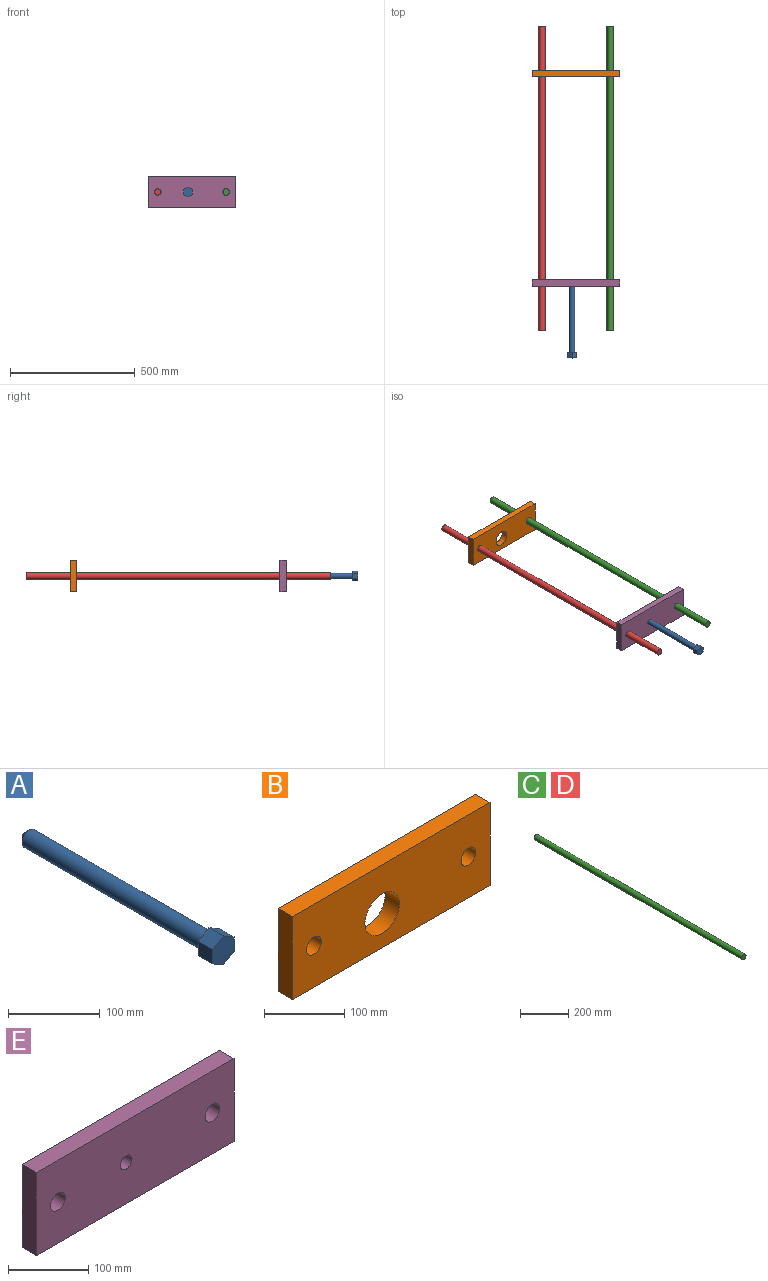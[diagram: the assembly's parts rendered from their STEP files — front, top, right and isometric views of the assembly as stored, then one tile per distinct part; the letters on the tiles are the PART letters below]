
ASSEMBLY  parts=5 mates=4
PART A: 11 faces, bbox 33.3x304.8x38.5 mm
  f0: cylinder r=11.11mm len=276.62mm, axis (0,1,0), area 19314.3mm2, adj f7,f9
  f1: plane 21.83x16.67mm, normal (0.5,0,0.87), area 420.1mm2, adj f2,f6,f7,f8
  f2: plane 21.83x16.67mm, normal (-0.5,0,0.87), area 420.1mm2, adj f1,f3,f7,f8
  f3: plane 21.83x19.25mm, normal (-1,0,0), area 420.1mm2, adj f2,f4,f7,f8
  f4: plane 21.83x16.67mm, normal (-0.5,0,-0.87), area 420.1mm2, adj f3,f5,f7,f8
  f5: plane 21.83x16.67mm, normal (0.5,0,-0.87), area 420.1mm2, adj f4,f6,f7,f8
  f6: plane 21.83x19.25mm, normal (1,0,0), area 420.1mm2, adj f1,f5,f7,f8
  f7: plane 38.5x33.34mm, normal (0,1,0), area 574.5mm2, adj f0,f1,f2,f3,f4,f5,f6
  f8: plane 38.5x33.34mm, normal (0,-1,0), area 962.5mm2, adj f1,f2,f3,f4,f5,f6
  f9: cone r=11.11mm half-angle=45deg, axis (0,-1,0), area 447.9mm2, adj f0,f10
  f10: plane 9.53x9.53mm, normal (0,1,0), area 71.3mm2, adj f9
PART B: 9 faces, bbox 349.3x25.4x127 mm
  f0: plane 349.25x25.4mm, normal (0,0,-1), area 8870.9mm2, adj f1,f6,f7,f8
  f1: plane 127x25.4mm, normal (1,0,0), area 3225.8mm2, adj f0,f2,f7,f8
  f2: plane 349.25x25.4mm, normal (0,0,1), area 8870.9mm2, adj f1,f6,f7,f8
  f3: cylinder r=13.09mm len=26.19mm, axis (0,1,0), area 2089.7mm2, adj f7,f8
  f4: cylinder r=13.09mm len=26.19mm, axis (0,1,0), area 2089.7mm2, adj f7,f8
  f5: cylinder r=30.48mm len=60.96mm, axis (0,1,0), area 4864.4mm2, adj f7,f8
  f6: plane 127x25.4mm, normal (-1,0,0), area 3225.8mm2, adj f0,f2,f7,f8
  f7: plane 349.25x127mm, normal (0,-1,0), area 40358.9mm2, adj f0,f1,f2,f3,f4,f5,f6
  f8: plane 349.25x127mm, normal (0,1,0), area 40358.9mm2, adj f0,f1,f2,f3,f4,f5,f6
PART C: 3 faces, bbox 25.4x1219.2x25.4 mm
  f0: cylinder r=12.7mm len=1219.2mm, axis (0,1,0), area 97287.8mm2, adj f1,f2
  f1: plane 25.4x25.4mm, normal (0,-1,0), area 506.7mm2, adj f0
  f2: plane 25.4x25.4mm, normal (0,1,0), area 506.7mm2, adj f0
PART D: same geometry as C
PART E: 9 faces, bbox 349.3x25.4x127 mm
  f0: plane 349.25x25.4mm, normal (0,0,-1), area 8870.9mm2, adj f1,f6,f7,f8
  f1: plane 127x25.4mm, normal (1,0,0), area 3225.8mm2, adj f0,f2,f7,f8
  f2: plane 349.25x25.4mm, normal (0,0,1), area 8870.9mm2, adj f1,f6,f7,f8
  f3: cylinder r=13.11mm len=26.21mm, axis (0,1,0), area 2091.7mm2, adj f7,f8
  f4: cylinder r=13.11mm len=26.21mm, axis (0,1,0), area 2091.7mm2, adj f7,f8
  f5: cylinder r=10.31mm len=25.4mm, axis (0,1,0), area 1645.8mm2, adj f7,f8
  f6: plane 127x25.4mm, normal (-1,0,0), area 3225.8mm2, adj f0,f2,f7,f8
  f7: plane 349.25x127mm, normal (0,-1,0), area 42941.3mm2, adj f0,f1,f2,f3,f4,f5,f6
  f8: plane 349.25x127mm, normal (0,1,0), area 42941.3mm2, adj f0,f1,f2,f3,f4,f5,f6
PLACE A rot(axis=(0,1,0),180deg) t=(-37.47,-268.68,-12.57)mm
PLACE B rot(axis=(0,-1,0),0deg) t=(-21.59,577.25,-12.57)mm
PLACE C t=(114.93,145.45,-12.57)mm
PLACE D t=(-158.12,145.45,-12.57)mm
PLACE E t=(-21.59,-260.95,-12.57)mm fixed
MATE slider A.f0 <-> E.f5  axis (0,1,0) through (-37.47,-413.35,-12.57)mm
MATE parallel E.f2 <-> B.f2  axis (0,0,1) through (-21.59,-260.95,50.93)mm
MATE slider D.f0 <-> E.f3  axis (0,1,0) through (-158.12,145.45,-12.57)mm
MATE slider C.f0 <-> E.f4  axis (0,1,0) through (114.93,145.45,-12.57)mm
